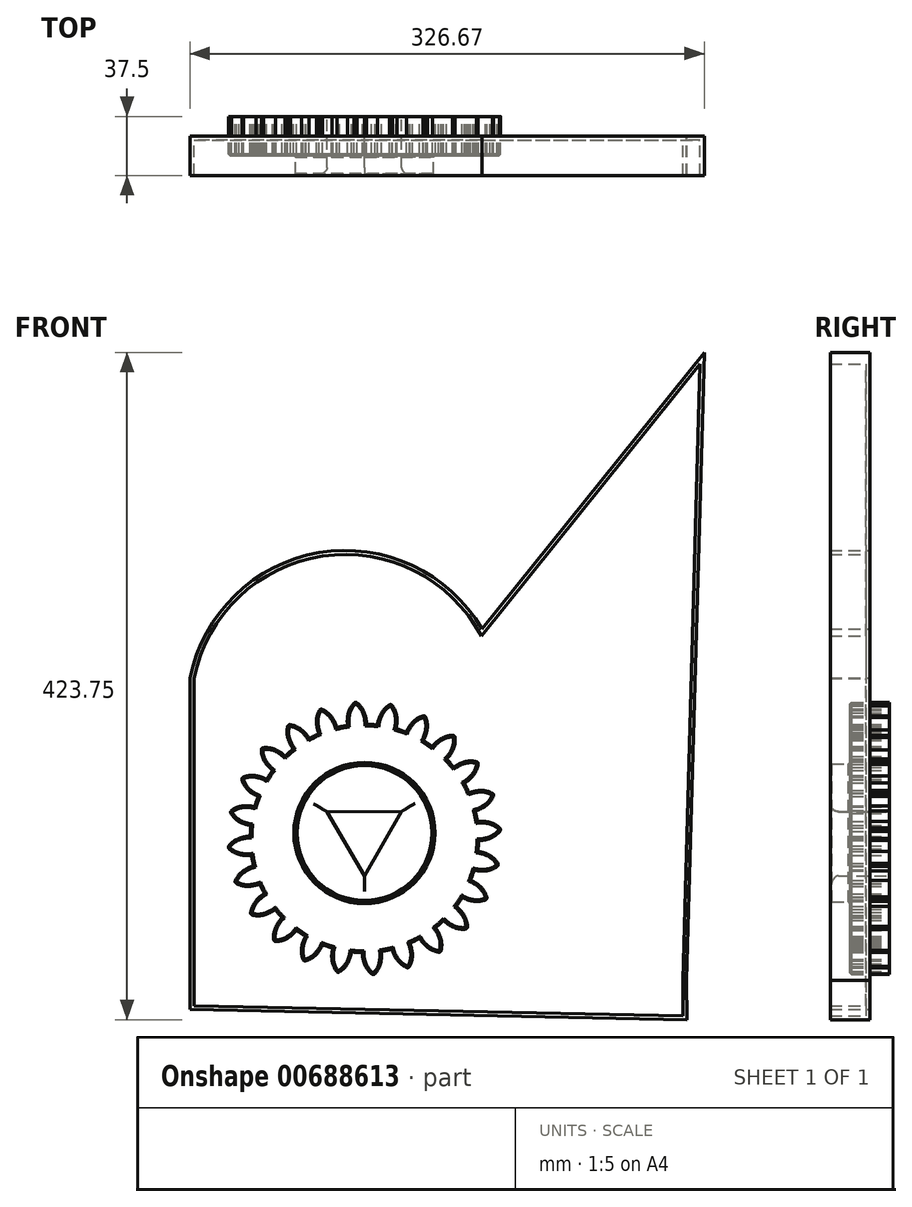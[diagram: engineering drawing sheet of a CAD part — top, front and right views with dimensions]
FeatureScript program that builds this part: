
annotation { "Feature Type Name" : "Feature", "Feature Type Description" : "" }
export const myFeature = defineFeature(function(context is Context, id is Id, definition is map)
    precondition{}
    {
        {
            var Q0;
            Q0=qCreatedBy(makeId("Front.planeOp"),FACE);
            var sketch = newSketch(context, id + "F0", { "sketchPlane" : qUnion([Q0])});
            skCircle(sketch, "E0", {"center": v(-0.05, -3.44) * mm, "radius": 86.16 * mm, "construction": true});
            skCircle(sketch, "E1", {"center": v(-0.05, -3.44) * mm, "radius": 79.67 * mm, "construction": true});
            skCircle(sketch, "E2", {"center": v(-0.05, -3.44) * mm, "radius": 72.52 * mm});
            skLineSegment(sketch, "E3", {"start": v(-0.05, -3.44) * mm, "end": v(-0.05, 109) * mm, "construction": true});
            skLineSegment(sketch, "E4", {"start": v(-0.05, -3.44) * mm, "end": v(-7.36, 108.12) * mm, "construction": true});
            skCircle(sketch, "E5", {"center": v(-0.05, -3.44) * mm, "radius": 74.83 * mm, "construction": true});
            skLineSegment(sketch, "E6", {"start": v(-0.05, 76.19) * mm, "end": v(-82.1, 46.32) * mm, "construction": true});
            skLineSegment(sketch, "E7", {"start": v(-0.05, 76.19) * mm, "end": v(-80.24, 76.19) * mm, "construction": true});
            skCircle(sketch, "E8", {"center": v(-0.05, 76.19) * mm, "radius": 14.6 * mm, "construction": true});
            skCircle(sketch, "E9", {"center": v(-13.78, 71.2) * mm, "radius": 14.6 * mm, "construction": true});
            skArc(sketch, "E10", {"start": v(-0.05, 76.19) * mm, "mid": v(-1.9, 79.7) * mm, "end": v(-4.65, 82.6) * mm});
            skArc(sketch, "E11.MirrorCS", {"start": v(-10.45, 75.5) * mm, "mid": v(-9.06, 79.24) * mm, "end": v(-6.73, 82.46) * mm});
            skArc(sketch, "E12", {"start": v(-4.65, 82.6) * mm, "mid": v(-5.72, 83) * mm, "end": v(-6.73, 82.46) * mm});
            skArc(sketch, "E13", {"start": v(-10.45, 75.5) * mm, "mid": v(-10.91, 71.91) * mm, "end": v(-10.77, 68.29) * mm});
            skArc(sketch, "E14", {"start": v(1.27, 69.07) * mm, "mid": v(0.96, 72.7) * mm, "end": v(-0.05, 76.19) * mm});
            skPoint(sketch, "E15.0.midPoint", {"position": v(-0.05, 17.48) * mm});
            skCircle(sketch, "E16", {"center": v(0, 0) * mm, "radius": 48.64 * mm});
            skCircle(sketch, "E17.cCircle", {"center": v(0, 0) * mm, "radius": 13.62 * mm, "construction": true});
            skLineSegment(sketch, "E17.0", {"start": v(-23.64, 13.53) * mm, "end": v(23.53, 13.7) * mm});
            skLineSegment(sketch, "E17.1", {"start": v(23.53, 13.7) * mm, "end": v(0.1, -27.23) * mm});
            skLineSegment(sketch, "E17.2", {"start": v(0.1, -27.23) * mm, "end": v(-23.64, 13.53) * mm});
            skPoint(sketch, "E17.0.midPoint", {"position": v(-0.05, 13.62) * mm});
            skSolve(sketch);
        }
        {
            var Q0;
            {var subQ0=sQuery(id+"F0.wireOp",EDGE,"E2");var subQ1=makeQuery(id+"F0.imprint","INTERSECT",VERTEX,{"derivedFrom":[subQ0,sQuery(id+"F0.wireOp",EDGE,"E13")]});Q0=makeQuery(id+"F0.imprint","IMPRINT",FACE,{"disambiguationData":[TD([[makeQuery(id+"F0.imprint","IMPRINT",EDGE,{"disambiguationData":[TD([[subQ1,1.0]])],"derivedFrom":subQ0}),1.0]])]});}
            var Q1;
            Q1=makeQuery(id+"F0.imprint","IMPRINT",FACE,{"disambiguationData":[TD([[makeQuery(id+"F0.imprint","IMPRINT",EDGE,{"derivedFrom":sQuery(id+"F0.wireOp",EDGE,"E10")}),1.0]])]});
            var Q2;
            Q2=makeQuery(id+"F0.imprint","IMPRINT",FACE,{"disambiguationData":[TD([[makeQuery(id+"F0.imprint","IMPRINT",EDGE,{"derivedFrom":sQuery(id+"F0.wireOp",EDGE,"E16")}),1.0]])]});
            extrude(context, id + "F1", {"entities" : qUnion([Q0, Q1, Q2]), "endBound" : BoundingType.SYMMETRIC, "depth" : 25 * mm, "offsetDistance" : 25 * mm});
        }
        {
            var Q0;
            Q0=makeQuery(id+"F1.opExtrude","SWEPT_BODY",BODY,{"disambiguationData":[OSD([sQuery(id+"F0.wireOp",EDGE,"E2"),sQuery(id+"F0.wireOp",EDGE,"E10"),sQuery(id+"F0.wireOp",EDGE,"E11.MirrorCS"),sQuery(id+"F0.wireOp",EDGE,"E12"),sQuery(id+"F0.wireOp",EDGE,"E13"),sQuery(id+"F0.wireOp",EDGE,"E14")])]});
            var Q1;
            Q1=makeQuery(id+"F1.opExtrude","SWEPT_FACE",FACE,{"disambiguationData":[OSD([sQuery(id+"F0.wireOp",EDGE,"E2")])]});
            circularPattern(context, id + "F2", {"entities" : qUnion([Q0]), "axis" : qUnion([Q1]), "angle" : 360 * degree, "instanceCount" : 24, "equalSpace" : true});
        }
        {
            var Q0;
            Q0=makeQuery(id+"F1.opExtrude","CAP_FACE",FACE,{"disambiguationData":[OSD([sQuery(id+"F0.wireOp",EDGE,"E2"),sQuery(id+"F0.wireOp",EDGE,"E10"),sQuery(id+"F0.wireOp",EDGE,"E11.MirrorCS"),sQuery(id+"F0.wireOp",EDGE,"E12"),sQuery(id+"F0.wireOp",EDGE,"E13"),sQuery(id+"F0.wireOp",EDGE,"E14"),sQuery(id+"F0.wireOp",EDGE,"E17.0"),sQuery(id+"F0.wireOp",EDGE,"E17.1"),sQuery(id+"F0.wireOp",EDGE,"E17.2")])],"isStart":false});
            var sketch = newSketch(context, id + "F3", { "sketchPlane" : qUnion([Q0])});
            skCircle(sketch, "E18", {"center": v(0, 0) * mm, "radius": 43.85 * mm});
            skSolve(sketch);
        }
        {
            var Q0;
            Q0=makeQuery(id+"F3.imprint","IMPRINT",FACE,{"disambiguationData":[TD([[makeQuery(id+"F3.imprint","IMPRINT",EDGE,{"derivedFrom":sQuery(id+"F3.wireOp",EDGE,"E18")}),1.0]])]});
            extrude(context, id + "F4", {"entities" : qUnion([Q0]), "operationType" : NewBodyOperationType.ADD, "endBound" : BoundingType.SYMMETRIC, "depth" : 25 * mm, "offsetDistance" : 25 * mm});
        }
        {
            var Q0;
            Q0=makeQuery(id+"F4.opExtrude","CAP_EDGE",EDGE,{"disambiguationData":[OSD([sQuery(id+"F0.wireOp",EDGE,"E17.0")])],"isStart":false});
            var Q1;
            Q1=makeQuery(id+"F4.opExtrude","CAP_EDGE",EDGE,{"disambiguationData":[OSD([sQuery(id+"F0.wireOp",EDGE,"E17.2")])],"isStart":false});
            var Q2;
            Q2=makeQuery(id+"F4.opExtrude","CAP_EDGE",EDGE,{"disambiguationData":[OSD([sQuery(id+"F0.wireOp",EDGE,"E17.1")])],"isStart":false});
            fillet(context, id + "F5", {"entities" : qUnion([Q0, Q1, Q2]), "radius" : 5 * mm, "tangentPropagation" : true, "allowEdgeOverflow" : false});
        }
        {
            var Q0;
            {var subQ0=makeQuery(id+"F1.opExtrude","CAP_FACE",FACE,{"disambiguationData":[OSD([sQuery(id+"F0.wireOp",EDGE,"E2"),sQuery(id+"F0.wireOp",EDGE,"E10"),sQuery(id+"F0.wireOp",EDGE,"E11.MirrorCS"),sQuery(id+"F0.wireOp",EDGE,"E12"),sQuery(id+"F0.wireOp",EDGE,"E13"),sQuery(id+"F0.wireOp",EDGE,"E14"),sQuery(id+"F0.wireOp",EDGE,"E17.0"),sQuery(id+"F0.wireOp",EDGE,"E17.1"),sQuery(id+"F0.wireOp",EDGE,"E17.2")])],"isStart":false});Q0=makeQuery(id+"F4.boolean.opBoolean","MERGE",FACE,{"derivedFrom":[makeQuery(id+"F2.opPattern","COPY",FACE,{"derivedFrom":subQ0,"instanceName":"1"}),makeQuery(id+"F2.opPattern","COPY",FACE,{"derivedFrom":subQ0,"instanceName":"2"}),makeQuery(id+"F2.opPattern","COPY",FACE,{"derivedFrom":subQ0,"instanceName":"3"}),makeQuery(id+"F2.opPattern","COPY",FACE,{"derivedFrom":subQ0,"instanceName":"4"}),makeQuery(id+"F2.opPattern","COPY",FACE,{"derivedFrom":subQ0,"instanceName":"5"}),makeQuery(id+"F2.opPattern","COPY",FACE,{"derivedFrom":subQ0,"instanceName":"6"}),makeQuery(id+"F2.opPattern","COPY",FACE,{"derivedFrom":subQ0,"instanceName":"7"}),makeQuery(id+"F2.opPattern","COPY",FACE,{"derivedFrom":subQ0,"instanceName":"8"}),makeQuery(id+"F2.opPattern","COPY",FACE,{"derivedFrom":subQ0,"instanceName":"9"}),makeQuery(id+"F2.opPattern","COPY",FACE,{"derivedFrom":subQ0,"instanceName":"10"}),makeQuery(id+"F2.opPattern","COPY",FACE,{"derivedFrom":subQ0,"instanceName":"11"}),makeQuery(id+"F2.opPattern","COPY",FACE,{"derivedFrom":subQ0,"instanceName":"12"}),makeQuery(id+"F2.opPattern","COPY",FACE,{"derivedFrom":subQ0,"instanceName":"13"}),makeQuery(id+"F2.opPattern","COPY",FACE,{"derivedFrom":subQ0,"instanceName":"14"}),makeQuery(id+"F2.opPattern","COPY",FACE,{"derivedFrom":subQ0,"instanceName":"15"}),makeQuery(id+"F2.opPattern","COPY",FACE,{"derivedFrom":subQ0,"instanceName":"16"}),makeQuery(id+"F2.opPattern","COPY",FACE,{"derivedFrom":subQ0,"instanceName":"17"}),makeQuery(id+"F2.opPattern","COPY",FACE,{"derivedFrom":subQ0,"instanceName":"18"}),makeQuery(id+"F2.opPattern","COPY",FACE,{"derivedFrom":subQ0,"instanceName":"19"}),makeQuery(id+"F2.opPattern","COPY",FACE,{"derivedFrom":subQ0,"instanceName":"20"}),makeQuery(id+"F2.opPattern","COPY",FACE,{"derivedFrom":subQ0,"instanceName":"21"}),makeQuery(id+"F2.opPattern","COPY",FACE,{"derivedFrom":subQ0,"instanceName":"22"}),makeQuery(id+"F2.opPattern","COPY",FACE,{"derivedFrom":subQ0,"instanceName":"23"})]});}
            extrude(context, id + "F6", {"entities" : qUnion([Q0]), "operationType" : NewBodyOperationType.REMOVE, "oppositeDirection" : true, "depth" : 30 * mm, "offsetDistance" : 25 * mm});
        }
        {
            var Q0;
            Q0=makeQuery(id+"F4.opExtrude","CAP_EDGE",EDGE,{"disambiguationData":[OSD([sQuery(id+"F3.wireOp",EDGE,"E18")])],"isStart":false});
            var Q1;
            {var subQ0=makeQuery(id+"F1.opExtrude","CAP_FACE",FACE,{"disambiguationData":[OSD([sQuery(id+"F0.wireOp",EDGE,"E2"),sQuery(id+"F0.wireOp",EDGE,"E10"),sQuery(id+"F0.wireOp",EDGE,"E11.MirrorCS"),sQuery(id+"F0.wireOp",EDGE,"E12"),sQuery(id+"F0.wireOp",EDGE,"E13"),sQuery(id+"F0.wireOp",EDGE,"E14"),sQuery(id+"F0.wireOp",EDGE,"E17.0"),sQuery(id+"F0.wireOp",EDGE,"E17.1"),sQuery(id+"F0.wireOp",EDGE,"E17.2")])],"isStart":false});Q1=makeQuery(id+"F4.boolean.opBoolean","MERGE",FACE,{"derivedFrom":[subQ0,makeQuery(id+"F2.opPattern","COPY",FACE,{"derivedFrom":subQ0,"instanceName":"1"}),makeQuery(id+"F2.opPattern","COPY",FACE,{"derivedFrom":subQ0,"instanceName":"2"}),makeQuery(id+"F2.opPattern","COPY",FACE,{"derivedFrom":subQ0,"instanceName":"3"}),makeQuery(id+"F2.opPattern","COPY",FACE,{"derivedFrom":subQ0,"instanceName":"4"}),makeQuery(id+"F2.opPattern","COPY",FACE,{"derivedFrom":subQ0,"instanceName":"5"}),makeQuery(id+"F2.opPattern","COPY",FACE,{"derivedFrom":subQ0,"instanceName":"6"}),makeQuery(id+"F2.opPattern","COPY",FACE,{"derivedFrom":subQ0,"instanceName":"7"}),makeQuery(id+"F2.opPattern","COPY",FACE,{"derivedFrom":subQ0,"instanceName":"8"}),makeQuery(id+"F2.opPattern","COPY",FACE,{"derivedFrom":subQ0,"instanceName":"9"}),makeQuery(id+"F2.opPattern","COPY",FACE,{"derivedFrom":subQ0,"instanceName":"10"}),makeQuery(id+"F2.opPattern","COPY",FACE,{"derivedFrom":subQ0,"instanceName":"11"}),makeQuery(id+"F2.opPattern","COPY",FACE,{"derivedFrom":subQ0,"instanceName":"12"}),makeQuery(id+"F2.opPattern","COPY",FACE,{"derivedFrom":subQ0,"instanceName":"13"}),makeQuery(id+"F2.opPattern","COPY",FACE,{"derivedFrom":subQ0,"instanceName":"14"}),makeQuery(id+"F2.opPattern","COPY",FACE,{"derivedFrom":subQ0,"instanceName":"15"}),makeQuery(id+"F2.opPattern","COPY",FACE,{"derivedFrom":subQ0,"instanceName":"16"}),makeQuery(id+"F2.opPattern","COPY",FACE,{"derivedFrom":subQ0,"instanceName":"17"}),makeQuery(id+"F2.opPattern","COPY",FACE,{"derivedFrom":subQ0,"instanceName":"18"}),makeQuery(id+"F2.opPattern","COPY",FACE,{"derivedFrom":subQ0,"instanceName":"19"}),makeQuery(id+"F2.opPattern","COPY",FACE,{"derivedFrom":subQ0,"instanceName":"20"}),makeQuery(id+"F2.opPattern","COPY",FACE,{"derivedFrom":subQ0,"instanceName":"21"}),makeQuery(id+"F2.opPattern","COPY",FACE,{"derivedFrom":subQ0,"instanceName":"22"}),makeQuery(id+"F2.opPattern","COPY",FACE,{"derivedFrom":subQ0,"instanceName":"23"})]});}
            chamfer(context, id + "F7", {"entities" : qUnion([Q0, Q1]), "width" : 1 * mm, "tangentPropagation" : true});
        }
        {
            var Q0;
            Q0=qCreatedBy(makeId("Front.planeOp"),FACE);
            var sketch = newSketch(context, id + "F8", { "sketchPlane" : qUnion([Q0])});
            skLineSegment(sketch, "E19", {"start": v(-110.79, -80.06) * mm, "end": v(-110.79, 98.47) * mm});
            skArc(sketch, "E20", {"start": v(74.54, 129.7) * mm, "mid": v(-28.9, 178.03) * mm, "end": v(-110.79, 98.47) * mm});
            skLineSegment(sketch, "E21", {"start": v(74.54, 129.7) * mm, "end": v(215.88, 305.2) * mm});
            skLineSegment(sketch, "E22", {"start": v(215.88, 305.2) * mm, "end": v(204.64, -93.68) * mm});
            skLineSegment(sketch, "E23", {"start": v(-110.79, -80.06) * mm, "end": v(-110.79, -112.14) * mm});
            skLineSegment(sketch, "E24", {"start": v(-110.79, -112.14) * mm, "end": v(204.66, -118.56) * mm});
            skLineSegment(sketch, "E25", {"start": v(204.64, -93.68) * mm, "end": v(204.66, -118.56) * mm});
            skSolve(sketch);
        }
        {
            var Q0;
            Q0=makeQuery(id+"F8.imprint","IMPRINT",FACE,{"disambiguationData":[TD([[makeQuery(id+"F8.imprint","IMPRINT",EDGE,{"derivedFrom":sQuery(id+"F8.wireOp",EDGE,"E19")}),-1.0]])]});
            extrude(context, id + "F9", {"entities" : qUnion([Q0]), "depth" : 25 * mm, "offsetDistance" : 25 * mm});
        }
        {
            var Q0;
            Q0=makeQuery(id+"F9.opExtrude","CAP_FACE",FACE,{"disambiguationData":[OSD([sQuery(id+"F8.wireOp",EDGE,"E19"),sQuery(id+"F8.wireOp",EDGE,"E20"),sQuery(id+"F8.wireOp",EDGE,"E21"),sQuery(id+"F8.wireOp",EDGE,"E22"),sQuery(id+"F8.wireOp",EDGE,"E23"),sQuery(id+"F8.wireOp",EDGE,"E24"),sQuery(id+"F8.wireOp",EDGE,"E25")])],"isStart":false});
            shell(context, id + "F10", {"entities" : qUnion([Q0]), "thickness" : 2.5 * mm});
        }
    });
